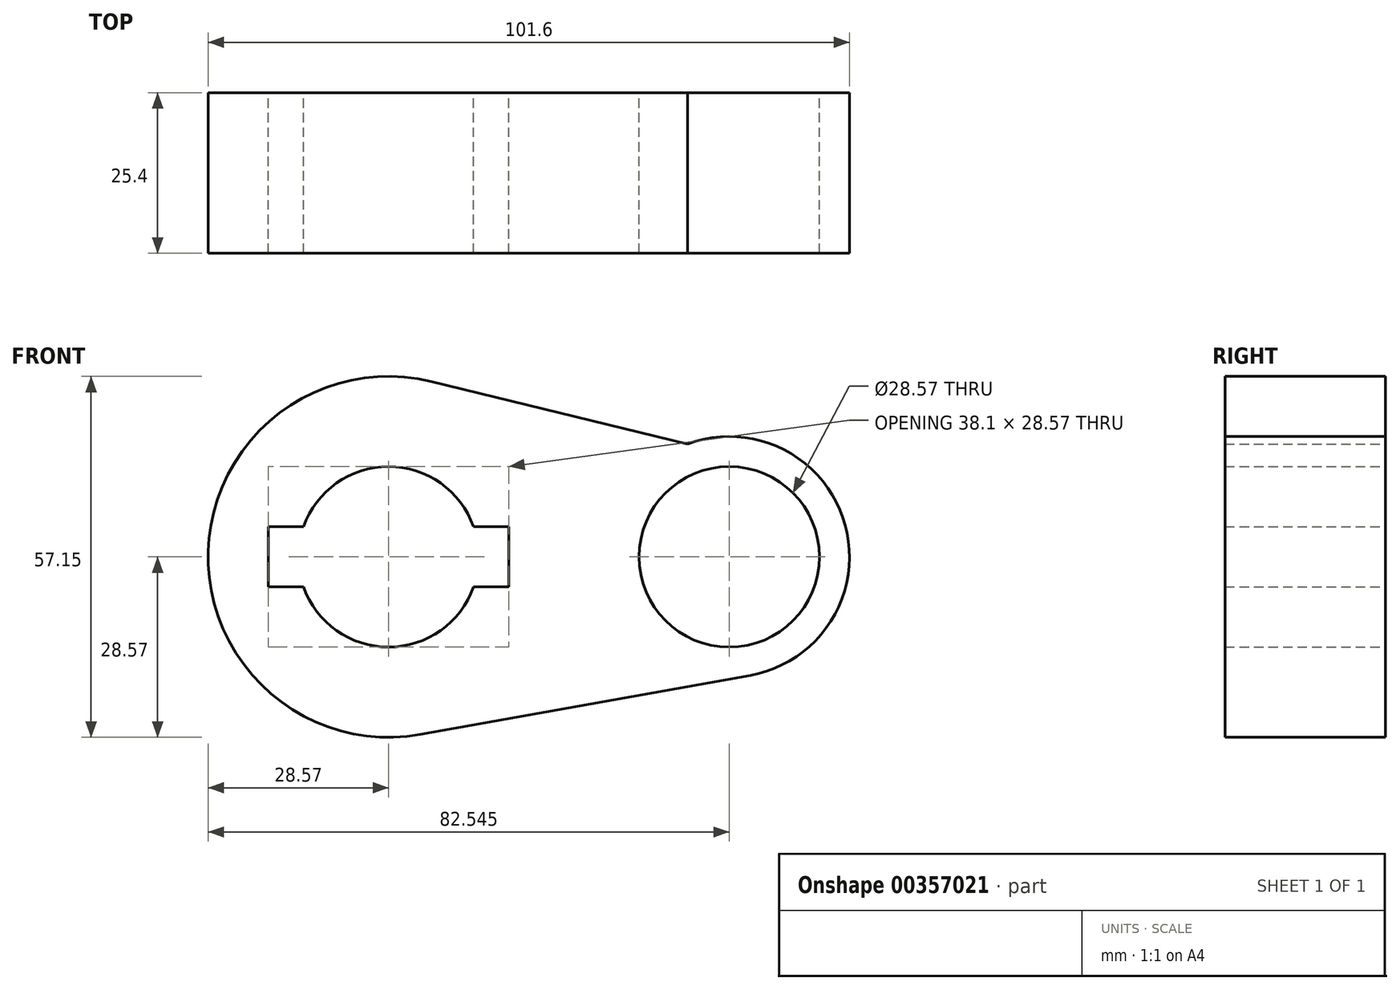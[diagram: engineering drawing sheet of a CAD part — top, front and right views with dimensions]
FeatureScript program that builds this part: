
annotation { "Feature Type Name" : "Feature", "Feature Type Description" : "" }
export const myFeature = defineFeature(function(context is Context, id is Id, definition is map)
    precondition{}
    {
        {
            var Q0;
            Q0=qCreatedBy(makeId("Front.planeOp"),FACE);
            var sketch = newSketch(context, id + "F0", { "sketchPlane" : qUnion([Q0])});
            skCircle(sketch, "E0", {"center": v(0, 0) * mm, "radius": 28.57 * mm});
            skCircle(sketch, "E1", {"center": v(53.98, 0) * mm, "radius": 19.05 * mm});
            skLineSegment(sketch, "E2", {"start": v(6.76, 27.76) * mm, "end": v(47.38, 17.87) * mm});
            skLineSegment(sketch, "E3", {"start": v(5.04, -28.13) * mm, "end": v(57.34, -18.75) * mm});
            skCircle(sketch, "E4", {"center": v(0, 0) * mm, "radius": 14.29 * mm});
            skCircle(sketch, "E5", {"center": v(53.98, 0) * mm, "radius": 14.29 * mm});
            skLineSegment(sketch, "E6.bottom", {"start": v(19.05, -4.76) * mm, "end": v(-19.05, -4.76) * mm});
            skLineSegment(sketch, "E6.top", {"start": v(19.05, 4.76) * mm, "end": v(-19.05, 4.76) * mm});
            skLineSegment(sketch, "E6.left", {"start": v(19.05, -4.76) * mm, "end": v(19.05, 4.76) * mm});
            skLineSegment(sketch, "E6.right", {"start": v(-19.05, -4.76) * mm, "end": v(-19.05, 4.76) * mm});
            skSolve(sketch);
        }
        {
            var Q0;
            Q0 = qSketchRegion(id + "F0", true);
            extrude(context, id + "F1", {"entities" : qUnion([Q0]), "depth" : 25.4 * mm});
        }
    });
